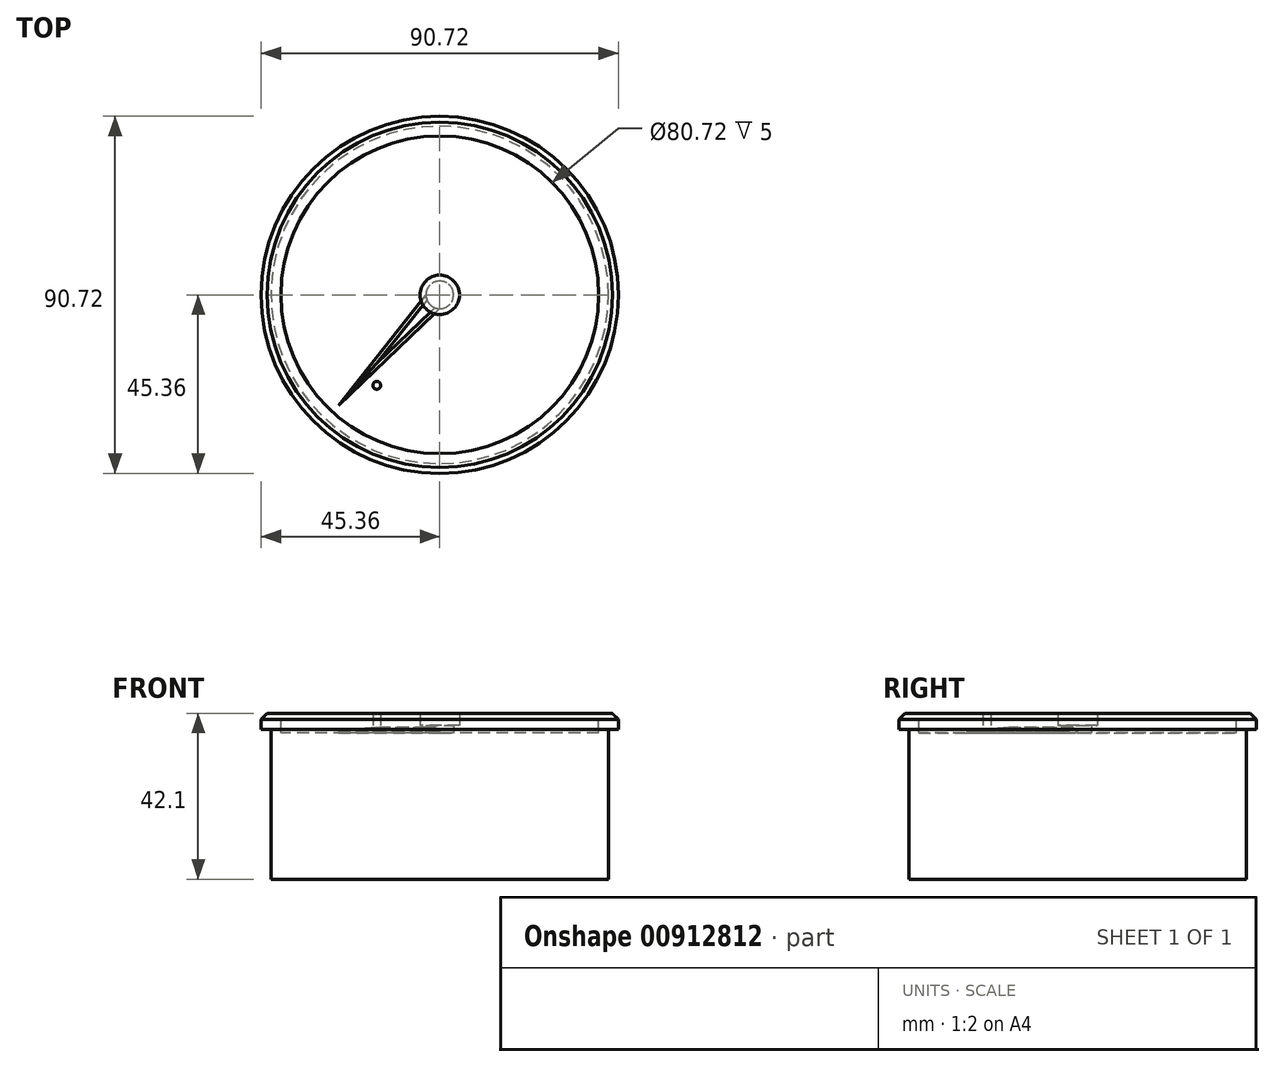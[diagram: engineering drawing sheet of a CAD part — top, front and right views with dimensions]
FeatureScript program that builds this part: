
annotation { "Feature Type Name" : "Feature", "Feature Type Description" : "" }
export const myFeature = defineFeature(function(context is Context, id is Id, definition is map)
    precondition{}
    {
        {
            var Q0;
            Q0=qCreatedBy(makeId("Top.planeOp"),FACE);
            var sketch = newSketch(context, id + "F0", { "sketchPlane" : qUnion([Q0])});
            skCircle(sketch, "E0", {"center": v(0, 0) * mm, "radius": 42.86 * mm});
            skSolve(sketch);
        }
        {
            var Q0;
            Q0=makeQuery(id+"F0.imprint","IMPRINT",FACE,{"disambiguationData":[TD([[makeQuery(id+"F0.imprint","IMPRINT",EDGE,{"derivedFrom":sQuery(id+"F0.wireOp",EDGE,"E0")}),1.0]])]});
            extrude(context, id + "F1", {"entities" : qUnion([Q0]), "depth" : 38.1 * mm, "offsetDistance" : 25 * mm});
        }
        {
            var Q0;
            Q0=makeQuery(id+"F1.opExtrude","CAP_FACE",FACE,{"disambiguationData":[OSD([sQuery(id+"F0.wireOp",EDGE,"E0")])],"isStart":false});
            var sketch = newSketch(context, id + "F2", { "sketchPlane" : qUnion([Q0])});
            skCircle(sketch, "E1", {"center": v(0, 0) * mm, "radius": 45.36 * mm});
            skSolve(sketch);
        }
        {
            var Q0;
            Q0 = qSketchRegion(id + "F2", true);
            extrude(context, id + "F3", {"entities" : qUnion([Q0]), "operationType" : NewBodyOperationType.ADD, "depth" : 4 * mm, "offsetDistance" : 25 * mm});
        }
        {
            var Q0;
            Q0=makeQuery(id+"F3.opExtrude","CAP_FACE",FACE,{"disambiguationData":[OSD([sQuery(id+"F2.wireOp",EDGE,"E1")])],"isStart":false});
            var sketch = newSketch(context, id + "F4", { "sketchPlane" : qUnion([Q0])});
            skCircle(sketch, "E2.0", {"center": v(0, 0) * mm, "radius": 40.36 * mm});
            skSolve(sketch);
        }
        {
            var Q0;
            Q0=makeQuery(id+"F4.imprint","IMPRINT",FACE,{"disambiguationData":[TD([[makeQuery(id+"F4.imprint","IMPRINT",EDGE,{"derivedFrom":sQuery(id+"F4.wireOp",EDGE,"E2.0")}),1.0]])]});
            extrude(context, id + "F5", {"entities" : qUnion([Q0]), "operationType" : NewBodyOperationType.REMOVE, "oppositeDirection" : true, "depth" : 5 * mm, "offsetDistance" : 25 * mm});
        }
        {
            var Q0;
            Q0=makeQuery(id+"F3.opExtrude","CAP_EDGE",EDGE,{"disambiguationData":[OSD([sQuery(id+"F2.wireOp",EDGE,"E1")])],"isStart":false});
            var Q1;
            Q1=makeQuery(id+"F5.boolean.opBoolean","COPY",EDGE,{"derivedFrom":makeQuery(id+"F5.opExtrude","CAP_EDGE",EDGE,{"disambiguationData":[OSD([sQuery(id+"F4.wireOp",EDGE,"E2.0")])],"isStart":true})});
            chamfer(context, id + "F6", {"entities" : qUnion([Q0, Q1]), "width" : 1.5 * mm, "tangentPropagation" : true});
        }
        {
            var Q0;
            Q0=makeQuery(id+"F5.boolean.opBoolean","COPY",FACE,{"derivedFrom":makeQuery(id+"F5.opExtrude","CAP_FACE",FACE,{"disambiguationData":[OSD([sQuery(id+"F4.wireOp",EDGE,"E2.0")])],"isStart":false})});
            var sketch = newSketch(context, id + "F7", { "sketchPlane" : qUnion([Q0])});
            skCircle(sketch, "E3", {"center": v(0, 0) * mm, "radius": 3.5 * mm});
            skSolve(sketch);
        }
        {
            var Q0;
            Q0=makeQuery(id+"F7.imprint","IMPRINT",FACE,{"disambiguationData":[TD([[makeQuery(id+"F7.imprint","IMPRINT",EDGE,{"derivedFrom":sQuery(id+"F7.wireOp",EDGE,"E3")}),1.0]])]});
            extrude(context, id + "F8", {"entities" : qUnion([Q0]), "operationType" : NewBodyOperationType.ADD, "depth" : 2 * mm, "offsetDistance" : 25 * mm});
        }
        {
            var Q0;
            Q0=makeQuery(id+"F8.opExtrude","CAP_FACE",FACE,{"disambiguationData":[OSD([sQuery(id+"F7.wireOp",EDGE,"E3")])],"isStart":false});
            var sketch = newSketch(context, id + "F9", { "sketchPlane" : qUnion([Q0])});
            skCircle(sketch, "E4", {"center": v(0, 0) * mm, "radius": 5 * mm});
            skSolve(sketch);
        }
        {
            var Q0;
            Q0 = qSketchRegion(id + "F9", true);
            extrude(context, id + "F10", {"entities" : qUnion([Q0]), "operationType" : NewBodyOperationType.ADD, "depth" : 3 * mm, "offsetDistance" : 25 * mm});
        }
        {
            var Q0;
            Q0=makeQuery(id+"F5.boolean.opBoolean","COPY",FACE,{"derivedFrom":makeQuery(id+"F5.opExtrude","CAP_FACE",FACE,{"disambiguationData":[OSD([sQuery(id+"F4.wireOp",EDGE,"E2.0")])],"isStart":false})});
            var sketch = newSketch(context, id + "F11", { "sketchPlane" : qUnion([Q0])});
            skLineSegment(sketch, "E5", {"start": v(-3.5, 0) * mm, "end": v(-25.72, -28.12) * mm});
            skLineSegment(sketch, "E6", {"start": v(-25.72, -28.12) * mm, "end": v(0, -3.5) * mm});
            skLineSegment(sketch, "E7", {"start": v(0, -3.5) * mm, "end": v(-3.5, 0) * mm});
            skSolve(sketch);
        }
        {
            var Q0;
            {var subQ0=sQuery(id+"F11.wireOp",EDGE,"E7");Q0=makeQuery(id+"F11.imprint","IMPRINT",FACE,{"disambiguationData":[TD([[makeQuery(id+"F11.imprint","IMPRINT",EDGE,{"derivedFrom":subQ0}),1.0]])]});}
            var Q1;
            {var subQ0=sQuery(id+"F11.wireOp",EDGE,"E5");Q1=makeQuery(id+"F11.imprint","IMPRINT",FACE,{"disambiguationData":[TD([[makeQuery(id+"F11.imprint","IMPRINT",EDGE,{"derivedFrom":subQ0}),1.0]])]});}
            extrude(context, id + "F12", {"entities" : qUnion([Q0, Q1]), "operationType" : NewBodyOperationType.ADD, "depth" : 1.5 * mm, "offsetDistance" : 25 * mm});
        }
        {
            var Q0;
            Q0=makeQuery(id+"F12.opExtrude","CAP_EDGE",EDGE,{"disambiguationData":[OSD([sQuery(id+"F11.wireOp",EDGE,"E6")])],"isStart":false});
            var Q1;
            Q1=makeQuery(id+"F12.opExtrude","CAP_EDGE",EDGE,{"disambiguationData":[OSD([sQuery(id+"F11.wireOp",EDGE,"E5")])],"isStart":false});
            chamfer(context, id + "F13", {"entities" : qUnion([Q0, Q1]), "width" : 1 * mm, "tangentPropagation" : true});
        }
        {
            var Q0;
            Q0=makeQuery(id+"F5.boolean.opBoolean","COPY",FACE,{"derivedFrom":makeQuery(id+"F5.opExtrude","CAP_FACE",FACE,{"disambiguationData":[OSD([sQuery(id+"F4.wireOp",EDGE,"E2.0")])],"isStart":false})});
            var sketch = newSketch(context, id + "F14", { "sketchPlane" : qUnion([Q0])});
            skCircle(sketch, "E8", {"center": v(-16, -23) * mm, "radius": 1 * mm});
            skSolve(sketch);
        }
        {
            var Q0;
            Q0 = qSketchRegion(id + "F14", true);
            extrude(context, id + "F15", {"entities" : qUnion([Q0]), "operationType" : NewBodyOperationType.ADD, "depth" : 5 * mm, "offsetDistance" : 25 * mm});
        }
    });
